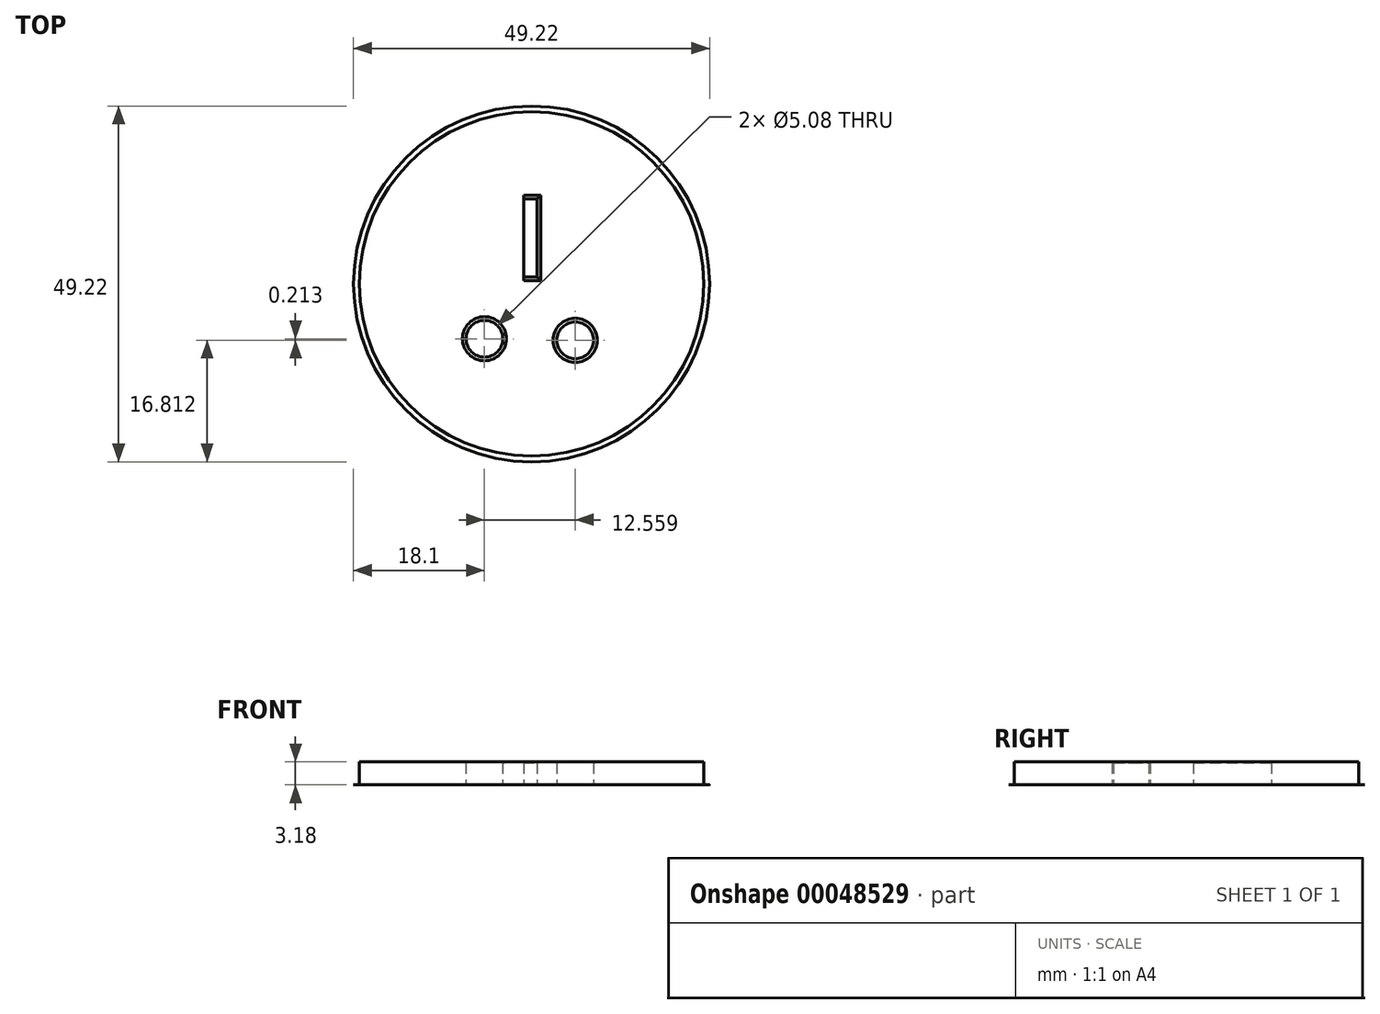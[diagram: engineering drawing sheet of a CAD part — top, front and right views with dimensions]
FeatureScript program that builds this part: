
annotation { "Feature Type Name" : "Feature", "Feature Type Description" : "" }
export const myFeature = defineFeature(function(context is Context, id is Id, definition is map)
    precondition{}
    {
        {
            var Q0;
            Q0=qCreatedBy(makeId("Top.planeOp"),FACE);
            var sketch = newSketch(context, id + "F0", { "sketchPlane" : qUnion([Q0])});
            skCircle(sketch, "E0", {"center": v(0, 0) * mm, "radius": 24.6 * mm});
            skSolve(sketch);
        }
        {
            var Q0;
            Q0=makeQuery(id+"F0.imprint","IMPRINT",FACE,{"disambiguationData":[TD([[makeQuery(id+"F0.imprint","IMPRINT",EDGE,{"derivedFrom":sQuery(id+"F0.wireOp",EDGE,"E0")}),1.0]])]});
            extrude(context, id + "F1", {"entities" : qUnion([Q0]), "depth" : 1 / 406.4 * mm});
        }
        {
            var Q0;
            Q0=qCreatedBy(makeId("Top.planeOp"),FACE);
            var sketch = newSketch(context, id + "F2", { "sketchPlane" : qUnion([Q0])});
            skCircle(sketch, "E1", {"center": v(0, 0) * mm, "radius": 23.81 * mm});
            skSolve(sketch);
        }
        {
            var Q0;
            Q0 = qSketchRegion(id + "F2", true);
            extrude(context, id + "F3", {"entities" : qUnion([Q0]), "operationType" : NewBodyOperationType.ADD, "depth" : 3.17 * mm});
        }
        {
            var Q0;
            Q0=qCreatedBy(makeId("Top.planeOp"),FACE);
            var sketch = newSketch(context, id + "F4", { "sketchPlane" : qUnion([Q0])});
            skCircle(sketch, "E2", {"center": v(-6.5, -7.58) * mm, "radius": 2.54 * mm});
            skSolve(sketch);
        }
        {
            var Q0;
            Q0=qCreatedBy(makeId("Top.planeOp"),FACE);
            var sketch = newSketch(context, id + "F5", { "sketchPlane" : qUnion([Q0])});
            skCircle(sketch, "E3", {"center": v(6.05, -7.8) * mm, "radius": 2.54 * mm});
            skSolve(sketch);
        }
        {
            var Q0;
            Q0=qCreatedBy(makeId("Top.planeOp"),FACE);
            var sketch = newSketch(context, id + "F6", { "sketchPlane" : qUnion([Q0])});
            skLineSegment(sketch, "E4.bottom", {"start": v(0.79, 0.93) * mm, "end": v(-1.1, 0.93) * mm});
            skLineSegment(sketch, "E4.top", {"start": v(0.79, 11.75) * mm, "end": v(-1.1, 11.75) * mm});
            skLineSegment(sketch, "E4.left", {"start": v(0.79, 0.93) * mm, "end": v(0.79, 11.75) * mm});
            skLineSegment(sketch, "E4.right", {"start": v(-1.1, 0.93) * mm, "end": v(-1.1, 11.75) * mm});
            skSolve(sketch);
        }
        {
            var Q0;
            Q0 = qSketchRegion(id + "F6", true);
            extrude(context, id + "F7", {"entities" : qUnion([Q0]), "operationType" : NewBodyOperationType.REMOVE, "endBound" : BoundingType.THROUGH_ALL, "depth" : 25.4 * mm});
        }
        {
            var Q0;
            Q0 = qSketchRegion(id + "F5", true);
            extrude(context, id + "F8", {"entities" : qUnion([Q0]), "operationType" : NewBodyOperationType.REMOVE, "endBound" : BoundingType.THROUGH_ALL, "depth" : 25.4 * mm});
        }
        {
            var Q0;
            Q0 = qSketchRegion(id + "F4", true);
            extrude(context, id + "F9", {"entities" : qUnion([Q0]), "operationType" : NewBodyOperationType.REMOVE, "endBound" : BoundingType.THROUGH_ALL, "depth" : 25.4 * mm});
        }
        {
            var Q0;
            Q0=makeQuery(id+"F7.boolean.opBoolean","COPY",EDGE,{"derivedFrom":makeQuery(id+"F7.opExtrude","CAP_EDGE",EDGE,{"disambiguationData":[OSD([sQuery(id+"F6.wireOp",EDGE,"E4.right")])],"isStart":true})});
            var Q1;
            Q1=makeQuery(id+"F7.boolean.opBoolean","INTERSECT",EDGE,{"derivedFrom":[makeQuery(id+"F3.opExtrude","CAP_FACE",FACE,{"disambiguationData":[OSD([sQuery(id+"F2.wireOp",EDGE,"E1")])],"isStart":false}),makeQuery(id+"F7.opExtrude","SWEPT_FACE",FACE,{"disambiguationData":[OSD([sQuery(id+"F6.wireOp",EDGE,"E4.left")])]})]});
            var Q2;
            Q2=makeQuery(id+"F7.boolean.opBoolean","INTERSECT",EDGE,{"derivedFrom":[makeQuery(id+"F3.opExtrude","CAP_FACE",FACE,{"disambiguationData":[OSD([sQuery(id+"F2.wireOp",EDGE,"E1")])],"isStart":false}),makeQuery(id+"F7.opExtrude","SWEPT_FACE",FACE,{"disambiguationData":[OSD([sQuery(id+"F6.wireOp",EDGE,"E4.top")])]})]});
            var Q3;
            Q3=makeQuery(id+"F7.boolean.opBoolean","INTERSECT",EDGE,{"derivedFrom":[makeQuery(id+"F3.opExtrude","CAP_FACE",FACE,{"disambiguationData":[OSD([sQuery(id+"F2.wireOp",EDGE,"E1")])],"isStart":false}),makeQuery(id+"F7.opExtrude","SWEPT_FACE",FACE,{"disambiguationData":[OSD([sQuery(id+"F6.wireOp",EDGE,"E4.bottom")])]})]});
            chamfer(context, id + "F10", {"entities" : qUnion([Q0, Q1, Q2, Q3]), "chamferType" : ChamferType.OFFSET_ANGLE, "width" : 0.5 * mm, "oppositeDirection" : false, "angle" : 15 * degree, "tangentPropagation" : true});
        }
        {
            var Q0;
            Q0=makeQuery(id+"F9.boolean.opBoolean","INTERSECT",EDGE,{"derivedFrom":[makeQuery(id+"F3.opExtrude","CAP_FACE",FACE,{"disambiguationData":[OSD([sQuery(id+"F2.wireOp",EDGE,"E1")])],"isStart":false}),makeQuery(id+"F9.opExtrude","SWEPT_FACE",FACE,{"disambiguationData":[OSD([sQuery(id+"F4.wireOp",EDGE,"E2")])]})]});
            chamfer(context, id + "F11", {"entities" : qUnion([Q0]), "chamferType" : ChamferType.OFFSET_ANGLE, "width" : 0.5 * mm, "oppositeDirection" : false, "angle" : 15 * degree, "tangentPropagation" : true});
        }
        {
            var Q0;
            Q0=makeQuery(id+"F8.boolean.opBoolean","INTERSECT",EDGE,{"derivedFrom":[makeQuery(id+"F3.opExtrude","CAP_FACE",FACE,{"disambiguationData":[OSD([sQuery(id+"F2.wireOp",EDGE,"E1")])],"isStart":false}),makeQuery(id+"F8.opExtrude","SWEPT_FACE",FACE,{"disambiguationData":[OSD([sQuery(id+"F5.wireOp",EDGE,"E3")])]})]});
            chamfer(context, id + "F12", {"entities" : qUnion([Q0]), "chamferType" : ChamferType.OFFSET_ANGLE, "width" : 0.5 * mm, "oppositeDirection" : false, "angle" : 15 * degree, "tangentPropagation" : true});
        }
    });
